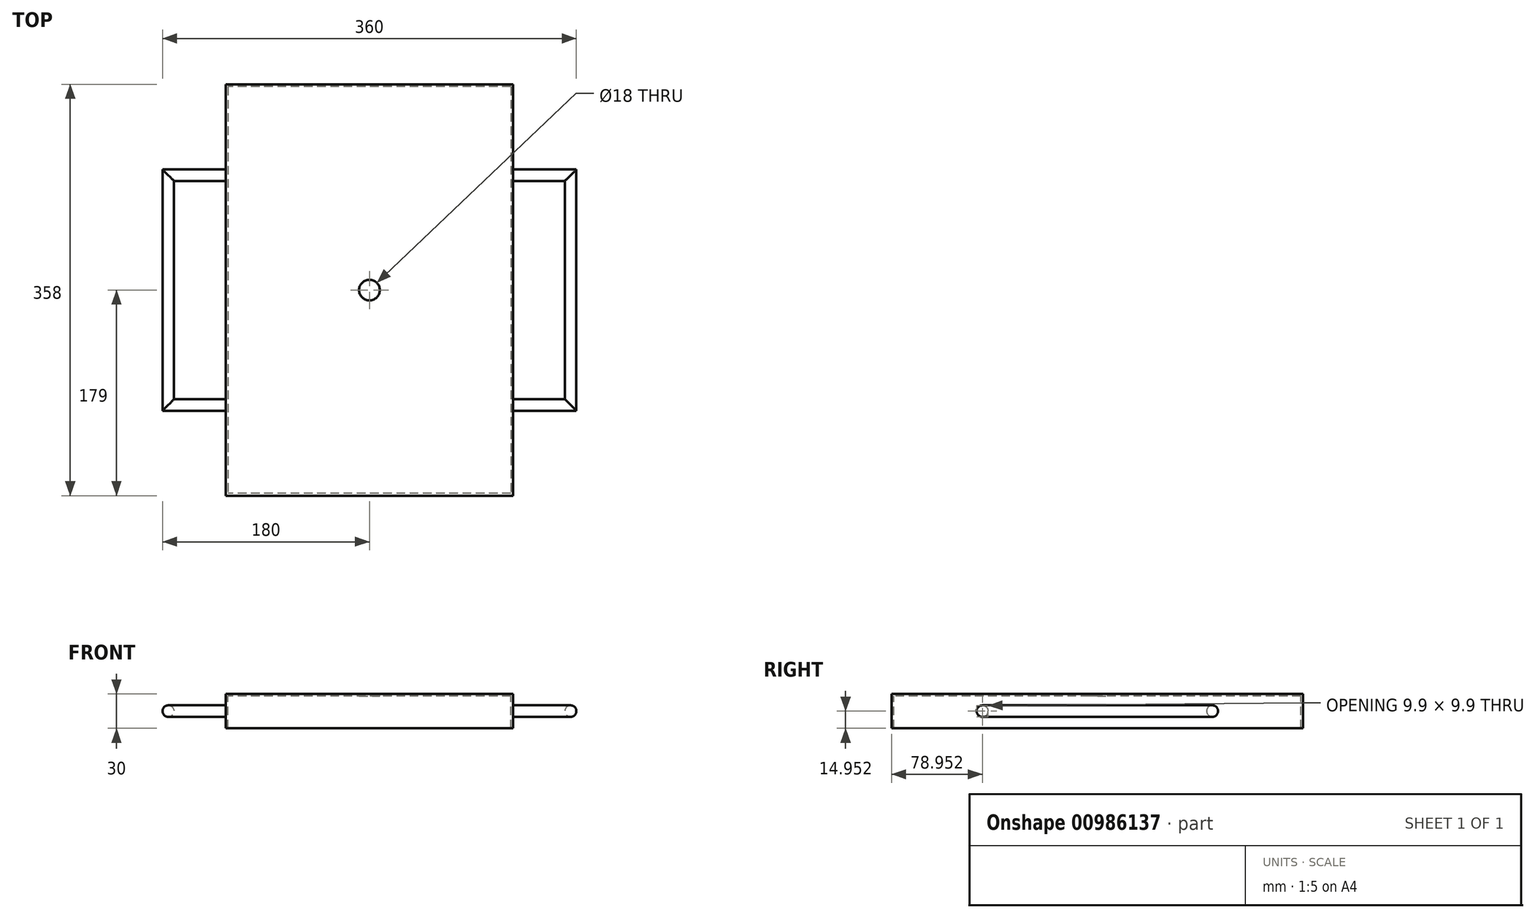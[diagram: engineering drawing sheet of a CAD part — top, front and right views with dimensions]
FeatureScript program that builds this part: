
annotation { "Feature Type Name" : "Feature", "Feature Type Description" : "" }
export const myFeature = defineFeature(function(context is Context, id is Id, definition is map)
    precondition{}
    {
        {
            var Q0;
            Q0=qCreatedBy(makeId("Right.planeOp"),FACE);
            var sketch = newSketch(context, id + "F0", { "sketchPlane" : qUnion([Q0])});
            skLineSegment(sketch, "E0", {"start": v(0, 0) * mm, "end": v(179, 0) * mm});
            skLineSegment(sketch, "E1", {"start": v(179, 0) * mm, "end": v(179, -30) * mm});
            skLineSegment(sketch, "E2", {"start": v(179, -30) * mm, "end": v(177, -30) * mm});
            skLineSegment(sketch, "E3", {"start": v(177, -30) * mm, "end": v(177, -2) * mm});
            skLineSegment(sketch, "E4", {"start": v(177, -2) * mm, "end": v(0, -2) * mm});
            skLineSegment(sketch, "E5", {"start": v(0, -2) * mm, "end": v(0, 0) * mm});
            skLineSegment(sketch, "E6.MirrorCS", {"start": v(0, 0) * mm, "end": v(-179, 0) * mm});
            skLineSegment(sketch, "E7.MirrorCS", {"start": v(-177, -2) * mm, "end": v(0, -2) * mm});
            skLineSegment(sketch, "E8.MirrorCS", {"start": v(-179, 0) * mm, "end": v(-179, -30) * mm});
            skLineSegment(sketch, "E9.MirrorCS", {"start": v(-177, -30) * mm, "end": v(-177, -2) * mm});
            skLineSegment(sketch, "E10.MirrorCS", {"start": v(-179, -30) * mm, "end": v(-177, -30) * mm});
            skSolve(sketch);
        }
        {
            var Q0;
            Q0=makeQuery(id+"F0.imprint","IMPRINT",FACE,{"disambiguationData":[TD([[makeQuery(id+"F0.imprint","IMPRINT",EDGE,{"derivedFrom":sQuery(id+"F0.wireOp",EDGE,"E0")}),-1.0]])]});
            var Q1;
            Q1=makeQuery(id+"F0.imprint","IMPRINT",FACE,{"disambiguationData":[TD([[makeQuery(id+"F0.imprint","IMPRINT",EDGE,{"derivedFrom":sQuery(id+"F0.wireOp",EDGE,"E5")}),1.0]])]});
            extrude(context, id + "F1", {"entities" : qUnion([Q0, Q1]), "depth" : 125 * mm, "offsetDistance" : 25 * mm});
        }
        {
            var Q0;
            Q0=makeQuery(id+"F1.opExtrude","CAP_FACE",FACE,{"disambiguationData":[OSD([sQuery(id+"F0.wireOp",EDGE,"E0"),sQuery(id+"F0.wireOp",EDGE,"E1"),sQuery(id+"F0.wireOp",EDGE,"E2"),sQuery(id+"F0.wireOp",EDGE,"E3"),sQuery(id+"F0.wireOp",EDGE,"E4"),sQuery(id+"F0.wireOp",EDGE,"E6.MirrorCS"),sQuery(id+"F0.wireOp",EDGE,"E7.MirrorCS"),sQuery(id+"F0.wireOp",EDGE,"E8.MirrorCS"),sQuery(id+"F0.wireOp",EDGE,"E9.MirrorCS"),sQuery(id+"F0.wireOp",EDGE,"E10.MirrorCS")])],"isStart":false});
            cPlane(context, id + "F2", {"entities" : qUnion([Q0]), "cplaneType" : CPlaneType.OFFSET, "offset" : 0 * mm, "width" : 150 * mm, "height" : 150 * mm});
        }
        {
            var Q0;
            Q0=qCreatedBy(id+"F2.planeOp",FACE);
            var sketch = newSketch(context, id + "F3", { "sketchPlane" : qUnion([Q0])});
            skLineSegment(sketch, "E11", {"start": v(0, 0) * mm, "end": v(179, 0) * mm});
            skLineSegment(sketch, "E12", {"start": v(179, 0) * mm, "end": v(179, -30) * mm});
            skLineSegment(sketch, "E13", {"start": v(179, -30) * mm, "end": v(-179, -30) * mm});
            skLineSegment(sketch, "E14", {"start": v(-179, -30) * mm, "end": v(-179, 0) * mm});
            skLineSegment(sketch, "E15", {"start": v(-179, 0) * mm, "end": v(0, 0) * mm});
            skSolve(sketch);
        }
        {
            var Q0;
            Q0=makeQuery(id+"F3.imprint","IMPRINT",FACE,{"disambiguationData":[TD([[makeQuery(id+"F3.imprint","IMPRINT",EDGE,{"derivedFrom":sQuery(id+"F3.wireOp",EDGE,"E11")}),-1.0]])]});
            extrude(context, id + "F4", {"entities" : qUnion([Q0]), "operationType" : NewBodyOperationType.ADD, "oppositeDirection" : true, "depth" : 2 * mm, "offsetDistance" : 25 * mm});
        }
        {
            var Q0;
            Q0=qCreatedBy(id+"F2.planeOp",FACE);
            var sketch = newSketch(context, id + "F5", { "sketchPlane" : qUnion([Q0])});
            skLineSegment(sketch, "E16", {"start": v(0, 0) * mm, "end": v(0, -15) * mm});
            skLineSegment(sketch, "E17", {"start": v(0, -15) * mm, "end": v(100, -15) * mm});
            skCircle(sketch, "E18", {"center": v(100, -15) * mm, "radius": 5 * mm});
            skSolve(sketch);
        }
        {
            var Q0;
            Q0=makeQuery(id+"F1.opExtrude","SWEPT_FACE",FACE,{"disambiguationData":[OSD([sQuery(id+"F0.wireOp",EDGE,"E0"),sQuery(id+"F0.wireOp",EDGE,"E6.MirrorCS")])]});
            cPlane(context, id + "F6", {"entities" : qUnion([Q0]), "cplaneType" : CPlaneType.OFFSET, "offset" : 15 * mm, "oppositeDirection" : true, "width" : 150 * mm, "height" : 150 * mm});
        }
        {
            var Q0;
            Q0=qCreatedBy(id+"F6.planeOp",FACE);
            var sketch = newSketch(context, id + "F7", { "sketchPlane" : qUnion([Q0])});
            skLineSegment(sketch, "E19", {"start": v(125, 100) * mm, "end": v(175, 100) * mm});
            skLineSegment(sketch, "E20", {"start": v(175, 100) * mm, "end": v(175, -100) * mm});
            skLineSegment(sketch, "E21", {"start": v(125, -100) * mm, "end": v(175, -100) * mm});
            skSolve(sketch);
        }
        {
            var Q0;
            Q0=makeQuery(id+"F5.imprint","IMPRINT",FACE,{"disambiguationData":[TD([[makeQuery(id+"F5.imprint","IMPRINT",EDGE,{"derivedFrom":sQuery(id+"F5.wireOp",EDGE,"E18")}),1.0]])]});
            var Q1;
            Q1=sQuery(id+"F7.wireOp",EDGE,"E19");
            var Q2;
            Q2=sQuery(id+"F7.wireOp",EDGE,"E20");
            var Q3;
            Q3=sQuery(id+"F7.wireOp",EDGE,"E21");
            sweep(context, id + "F8", {"profiles" : qUnion([Q0]), "path" : qUnion([Q1, Q2, Q3])});
        }
        {
            var Q0;
            Q0=makeQuery(id+"F1.opExtrude","SWEPT_BODY",BODY,{"disambiguationData":[OSD([sQuery(id+"F0.wireOp",EDGE,"E0"),sQuery(id+"F0.wireOp",EDGE,"E1"),sQuery(id+"F0.wireOp",EDGE,"E2"),sQuery(id+"F0.wireOp",EDGE,"E3"),sQuery(id+"F0.wireOp",EDGE,"E4"),sQuery(id+"F0.wireOp",EDGE,"E6.MirrorCS"),sQuery(id+"F0.wireOp",EDGE,"E7.MirrorCS"),sQuery(id+"F0.wireOp",EDGE,"E8.MirrorCS"),sQuery(id+"F0.wireOp",EDGE,"E9.MirrorCS"),sQuery(id+"F0.wireOp",EDGE,"E10.MirrorCS")])]});
            var Q1;
            Q1=makeQuery(id+"F8.opSweep","SWEPT_BODY",BODY,{"disambiguationData":[OSD([sQuery(id+"F5.wireOp",EDGE,"E18"),sQuery(id+"F7.wireOp",EDGE,"E21")])]});
            var Q2;
            Q2=makeQuery(id+"F1.opExtrude","CAP_FACE",FACE,{"disambiguationData":[OSD([sQuery(id+"F0.wireOp",EDGE,"E0"),sQuery(id+"F0.wireOp",EDGE,"E1"),sQuery(id+"F0.wireOp",EDGE,"E2"),sQuery(id+"F0.wireOp",EDGE,"E3"),sQuery(id+"F0.wireOp",EDGE,"E4"),sQuery(id+"F0.wireOp",EDGE,"E6.MirrorCS"),sQuery(id+"F0.wireOp",EDGE,"E7.MirrorCS"),sQuery(id+"F0.wireOp",EDGE,"E8.MirrorCS"),sQuery(id+"F0.wireOp",EDGE,"E9.MirrorCS"),sQuery(id+"F0.wireOp",EDGE,"E10.MirrorCS")])],"isStart":true});
            mirror(context, id + "F9", {"operationType" : NewBodyOperationType.ADD, "entities" : qUnion([Q0, Q1]), "mirrorPlane" : qUnion([Q2])});
        }
        {
            var Q0;
            Q0=qCreatedBy(makeId("Top.planeOp"),FACE);
            var sketch = newSketch(context, id + "F10", { "sketchPlane" : qUnion([Q0])});
            skCircle(sketch, "E22", {"center": v(0, 0) * mm, "radius": 9 * mm});
            skSolve(sketch);
        }
        {
            var Q0;
            Q0=makeQuery(id+"F10.imprint","IMPRINT",FACE,{"disambiguationData":[TD([[makeQuery(id+"F10.imprint","IMPRINT",EDGE,{"derivedFrom":sQuery(id+"F10.wireOp",EDGE,"E22")}),1.0]])]});
            extrude(context, id + "F11", {"entities" : qUnion([Q0]), "operationType" : NewBodyOperationType.REMOVE, "oppositeDirection" : true, "depth" : 25 * mm, "offsetDistance" : 25 * mm});
        }
    });
